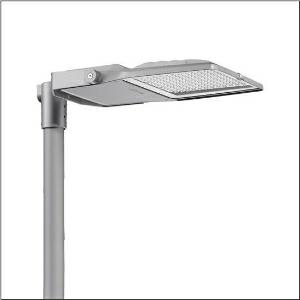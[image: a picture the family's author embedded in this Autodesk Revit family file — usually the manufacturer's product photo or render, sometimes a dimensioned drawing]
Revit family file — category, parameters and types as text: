
# Revit family: floodlight_fl_21_midi___pl52_5xa7781e4d3a_2d12
name_source: partatom
category: Lighting Fixtures
units: mm (PartAtom-declared; Revit-internal decimal feet)

## family parameters
Cut with Voids When Loaded = No
Host = Face
Light Source = No
Part Type = Normal
Room Calculation Point = No
Round Connector Dimension = Use Diameter
Shared = No

## types (1)
- --- (1 x LED, 28010 lm, 208.1 W, 4000K)
    Apparent Load = 208 VA
    CIE Flux Codes = 26 60 98 100 100
    Color Rendering = 70
    Color Temperature = 4000K
    Default Elevation = 1800 mm
    Description = Floodlight FL 21 midi, floodlight, primary light control with lens, of PMMA, primary optical cover: protective disc, of toughened safety glass, transparent, light distribution: PL52, light emission: direct distribution, installation type: surface-mounted, LED, High Power LED, rated luminous flux: 28.010lm, luminous efficacy: 134lm/W, light colour: 740, colour temperature: 4000K, control gear: ECG iQ, control: optimised constant luminous flux control (CLO 2.0), Desk-Remote (wireless, voltage-free reading and setting of iQ features in the workshop via application-optimized NFC function/RFID function), Light-Fading, Smart-Wire, Night-Set, Lumen-Switch, Temp-Guard, Auto-Match, with terminal, 6-pole, mains connection: 220..240V, AC, 50/60Hz, start of lifetime: 208W, end of lifetime: 227W, reduction: 90W, luminaire housing, of diecast aluminium, powder-coated, Siteco® metallic grey (DB 702S), corrosivity category C5 according to DIN EN ISO 12944, mast bracket, of steel, galvanised, powder-coated, Siteco® metallic grey (DB 702S), protection rating (complete): IP66, insulation class (complete): insulation class I (protective earthing), certification: CE, protection symbol: D, impact resistance: IK08, permissible operating ambient temperature: -40..+40°C, permissible operating ambient temperature for outdoor applications: -40..+50°C, standard: DIN EN 12944, packaging unit: 1 piece

Light Distribution: PL52
    Height = 76 mm
    Lamp = 1 x LED
    Lamp Light Flux = 28010 lm
    Lamp Power = 208.1 W
    Lamp count = 1
    Length = 657 mm
    Luminous efficacy = 135 lm/W
    Manufacturer = Siteco
    ModVariant = No
    Model = 5XA7781E4D3A
    Number of Poles = 1
    OnlyDefault = Yes
    Power Factor = 1
    Product Name = Floodlight FL 21 midi | PL52
    Product group = floodlight | pylon top
    ProductGroupID = 6101
    Protection Class = Protection class I
    Protection Degree = IP 66
    RLX_Detail_Level = 1
    RlxData = <blob elided: 153513 chars, md5=da29fcb7>
    Socket = socket
    Standby Power = 0 W
    System Light Flux = 28010 lm
    System Power = 208 W
    Type Comments = factory setting: luminous flux: 100 % | dim-lin: 254 | 710 mA
    Type Image = l_1007123.jpg
    URL = http://relux.com
    VarID = @adj_014805
    Voltage = 0 V
    Weight = 0.00 kg
    Width = 442 mm

## geometry (parser evidence)
native form markers: Blend x4, Sweep x15
no freeform markers — native parametric forms only
